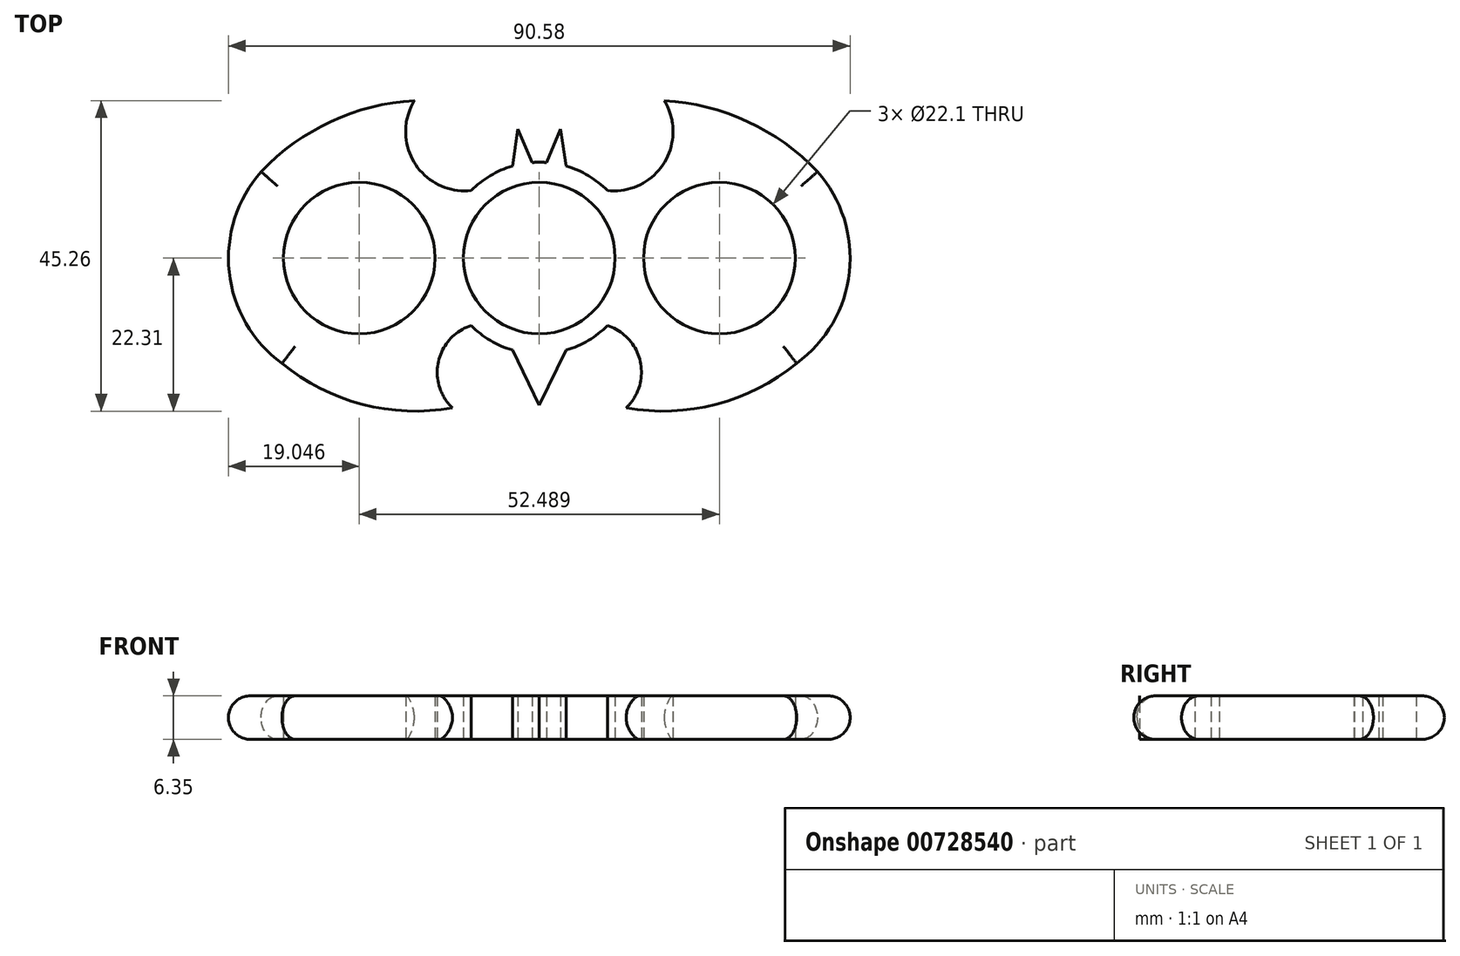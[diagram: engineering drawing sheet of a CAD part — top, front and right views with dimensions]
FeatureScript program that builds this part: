
annotation { "Feature Type Name" : "Feature", "Feature Type Description" : "" }
export const myFeature = defineFeature(function(context is Context, id is Id, definition is map)
    precondition{}
    {
        {
            var Q0;
            Q0=qCreatedBy(makeId("Top.planeOp"),FACE);
            var sketch = newSketch(context, id + "F0", { "sketchPlane" : qUnion([Q0])});
            skCircle(sketch, "E0", {"center": v(0, 0) * mm, "radius": 11.05 * mm});
            skCircle(sketch, "E1", {"center": v(0, 0) * mm, "radius": 13.97 * mm});
            skLineSegment(sketch, "E2", {"start": v(0, 0) * mm, "end": v(-26.24, 0) * mm});
            skCircle(sketch, "E3", {"center": v(-26.24, 0) * mm, "radius": 11.05 * mm});
            skLineSegment(sketch, "E4", {"start": v(0, 0) * mm, "end": v(26.24, 0) * mm});
            skCircle(sketch, "E5", {"center": v(26.24, 0) * mm, "radius": 11.05 * mm});
            skArc(sketch, "E6", {"start": v(37.5, -15.37) * mm, "mid": v(45.18, -2.05) * mm, "end": v(40.53, 12.6) * mm});
            skArc(sketch, "E7", {"start": v(-18.2, 22.95) * mm, "mid": v(-30.36, 19.9) * mm, "end": v(-40.53, 12.6) * mm});
            skArc(sketch, "E8", {"start": v(-18.2, 22.95) * mm, "mid": v(-18.15, 13.81) * mm, "end": v(-9.93, 9.83) * mm});
            skArc(sketch, "E9.trimOffspring", {"start": v(-40.53, 12.6) * mm, "mid": v(-45.18, -2.05) * mm, "end": v(-37.5, -15.37) * mm});
            skArc(sketch, "E10.MirrorCS", {"start": v(18.2, 22.95) * mm, "mid": v(18.15, 13.81) * mm, "end": v(9.93, 9.83) * mm});
            skArc(sketch, "E11.MirrorCS", {"start": v(18.2, 22.95) * mm, "mid": v(30.36, 19.9) * mm, "end": v(40.53, 12.6) * mm});
            skArc(sketch, "E12", {"start": v(-37.5, -15.37) * mm, "mid": v(-25.79, -21.32) * mm, "end": v(-12.65, -21.85) * mm});
            skArc(sketch, "E13", {"start": v(-9.93, -9.83) * mm, "mid": v(-14.7, -15.06) * mm, "end": v(-12.65, -21.85) * mm});
            skArc(sketch, "E14.MirrorCS", {"start": v(9.93, -9.83) * mm, "mid": v(14.7, -15.06) * mm, "end": v(12.65, -21.85) * mm});
            skArc(sketch, "E15.MirrorCS", {"start": v(37.5, -15.37) * mm, "mid": v(25.79, -21.32) * mm, "end": v(12.65, -21.85) * mm});
            skPoint(sketch, "E16.end.orphan", {"position": v(2.34, 18.82) * mm});
            skPoint(sketch, "E17.orphan", {"position": v(3.92, 13.4) * mm});
            skPoint(sketch, "E18.end.orphan", {"position": v(-1.04, 13.93) * mm});
            skPoint(sketch, "E19.end.orphan", {"position": v(-2.23, 18.82) * mm});
            skPoint(sketch, "E20.MirrorCS.end.orphan", {"position": v(1.04, 13.93) * mm});
            skPoint(sketch, "E20.MirrorCS.start.orphan", {"position": v(2.23, 18.82) * mm});
            skPoint(sketch, "E21.end.orphan", {"position": v(-4.8, 18.35) * mm});
            skPoint(sketch, "E22.MirrorCS.end.orphan", {"position": v(4.8, 18.35) * mm});
            skLineSegment(sketch, "E23", {"start": v(-1.04, 13.93) * mm, "end": v(-3.1, 18.83) * mm});
            skLineSegment(sketch, "E24", {"start": v(-3.1, 18.83) * mm, "end": v(-3.92, 13.4) * mm});
            skLineSegment(sketch, "E25.MirrorCS", {"start": v(1.04, 13.93) * mm, "end": v(3.1, 18.83) * mm});
            skLineSegment(sketch, "E26.MirrorCS", {"start": v(3.1, 18.83) * mm, "end": v(3.92, 13.4) * mm});
            skPoint(sketch, "E27.end.orphan", {"position": v(0, -21.45) * mm});
            skPoint(sketch, "E27.start.orphan", {"position": v(-4.01, -13.38) * mm});
            skPoint(sketch, "E28.MirrorCS.start.orphan", {"position": v(4.01, -13.38) * mm});
            skPoint(sketch, "E29.MirrorCS.end.orphan", {"position": v(-3.92, -13.4) * mm});
            skPoint(sketch, "E29.MirrorCS.start.orphan", {"position": v(-3.1, -18.83) * mm});
            skLineSegment(sketch, "E30", {"start": v(-3.92, -13.4) * mm, "end": v(0, -21.45) * mm});
            skLineSegment(sketch, "E31.MirrorCS", {"start": v(3.92, -13.4) * mm, "end": v(0, -21.45) * mm});
            skLineSegment(sketch, "E32", {"start": v(0, 0) * mm, "end": v(45.3, 0) * mm});
            skSolve(sketch);
        }
        {
            var Q0;
            Q0 = qSketchRegion(id + "F0", true);
            extrude(context, id + "F1", {"entities" : qUnion([Q0]), "depth" : 6.35 * mm, "offsetDistance" : 25.4 * mm});
        }
        {
            var Q0;
            Q0=makeQuery(id+"F1.opExtrude","CAP_EDGE",EDGE,{"disambiguationData":[OSD([sQuery(id+"F0.wireOp",EDGE,"E9.trimOffspring")])],"isStart":false});
            var Q1;
            Q1=makeQuery(id+"F1.opExtrude","CAP_EDGE",EDGE,{"disambiguationData":[OSD([sQuery(id+"F0.wireOp",EDGE,"E6")])],"isStart":false});
            var Q2;
            Q2=makeQuery(id+"F1.opExtrude","CAP_EDGE",EDGE,{"disambiguationData":[OSD([sQuery(id+"F0.wireOp",EDGE,"E6")])],"isStart":true});
            var Q3;
            Q3=makeQuery(id+"F1.opExtrude","CAP_EDGE",EDGE,{"disambiguationData":[OSD([sQuery(id+"F0.wireOp",EDGE,"E9.trimOffspring")])],"isStart":true});
            fillet(context, id + "F2", {"entities" : qUnion([Q0, Q1, Q2, Q3]), "radius" : 3.17 * mm, "tangentPropagation" : true, "allowEdgeOverflow" : false});
        }
    });
